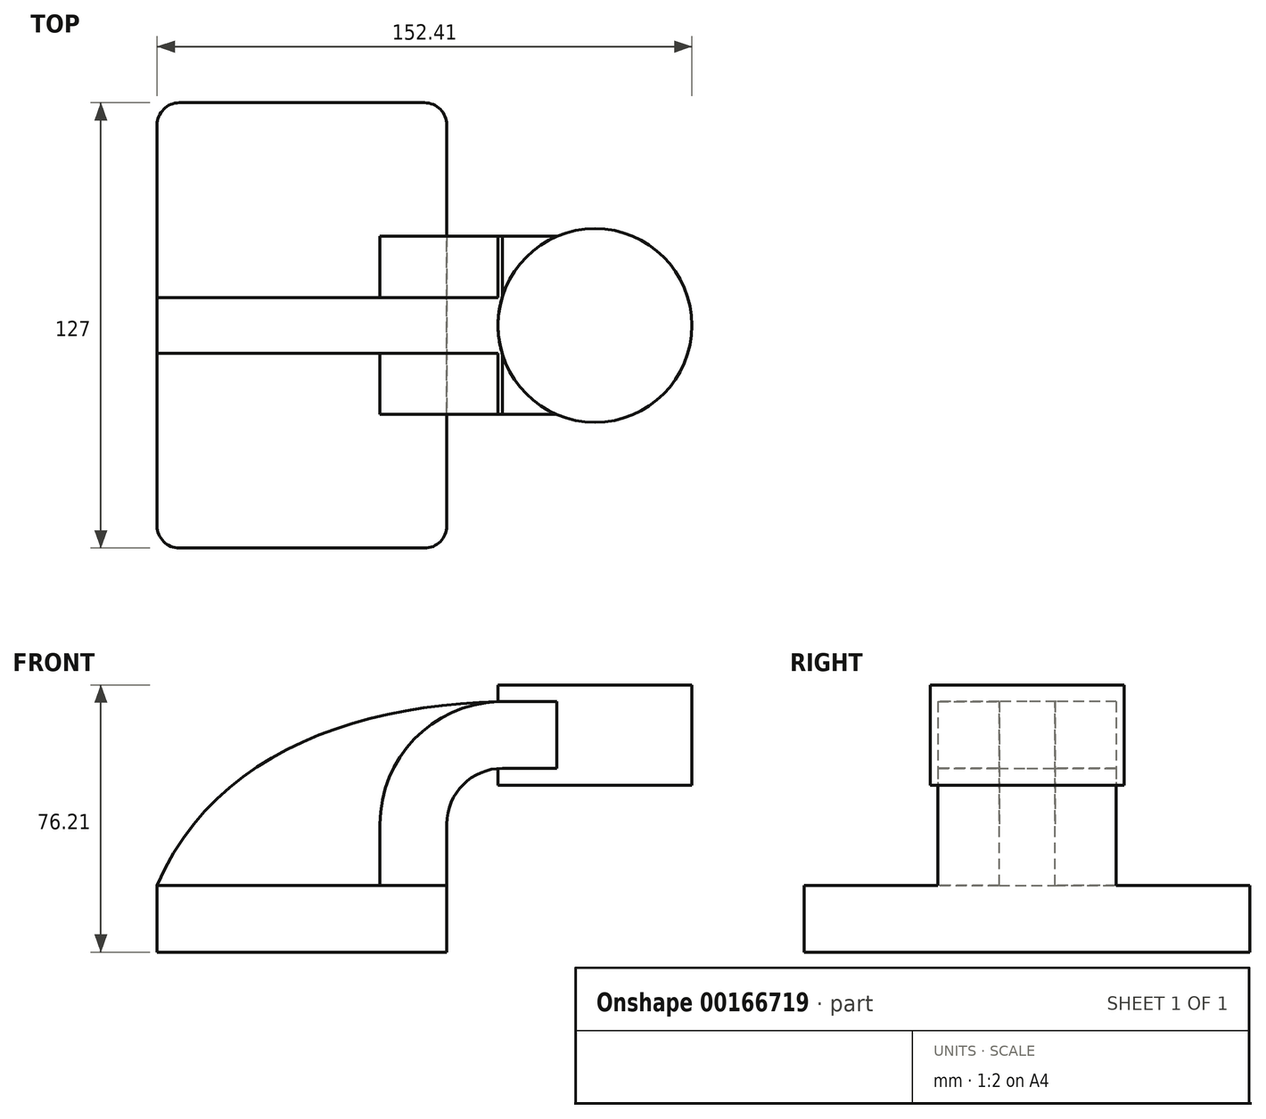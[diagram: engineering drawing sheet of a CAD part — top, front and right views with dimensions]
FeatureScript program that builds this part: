
annotation { "Feature Type Name" : "Feature", "Feature Type Description" : "" }
export const myFeature = defineFeature(function(context is Context, id is Id, definition is map)
    precondition{}
    {
        {
            var Q0;
            Q0=qCreatedBy(makeId("Front.planeOp"),FACE);
            var sketch = newSketch(context, id + "F0", { "sketchPlane" : qUnion([Q0])});
            skLineSegment(sketch, "E0.bottom", {"start": v(-41.28, 9.52) * mm, "end": v(41.27, 9.53) * mm});
            skLineSegment(sketch, "E0.top", {"start": v(-41.28, -9.53) * mm, "end": v(41.28, -9.53) * mm});
            skLineSegment(sketch, "E0.left", {"start": v(-41.28, 9.52) * mm, "end": v(-41.28, -9.53) * mm});
            skLineSegment(sketch, "E0.right", {"start": v(41.28, 9.53) * mm, "end": v(41.28, -9.52) * mm});
            skPoint(sketch, "E0.middle", {"position": v(0, 0) * mm});
            skLineSegment(sketch, "E1.bottom", {"start": v(60.32, 66.68) * mm, "end": v(111.12, 66.68) * mm});
            skLineSegment(sketch, "E1.top", {"start": v(60.32, 38.1) * mm, "end": v(111.12, 38.1) * mm});
            skLineSegment(sketch, "E1.left", {"start": v(60.32, 66.68) * mm, "end": v(60.32, 38.1) * mm});
            skLineSegment(sketch, "E1.right", {"start": v(111.12, 66.68) * mm, "end": v(111.12, 38.1) * mm});
            skPoint(sketch, "E1.middle", {"position": v(85.72, 52.39) * mm});
            skLineSegment(sketch, "E2", {"start": v(41.27, 9.53) * mm, "end": v(41.27, 27) * mm});
            skArc(sketch, "E3", {"start": v(41.27, 27) * mm, "mid": v(45.92, 38.23) * mm, "end": v(57.15, 42.88) * mm});
            skLineSegment(sketch, "E4", {"start": v(57.15, 42.88) * mm, "end": v(83.5, 42.88) * mm});
            skLineSegment(sketch, "E5.0", {"start": v(57.15, 61.93) * mm, "end": v(83.5, 61.93) * mm});
            skArc(sketch, "E5.1", {"start": v(22.22, 27) * mm, "mid": v(32.45, 51.7) * mm, "end": v(57.15, 61.93) * mm});
            skLineSegment(sketch, "E5.2", {"start": v(22.22, 9.53) * mm, "end": v(22.22, 27) * mm});
            skLineSegment(sketch, "E6", {"start": v(83.5, 38.1) * mm, "end": v(83.5, 66.68) * mm});
            skFitSpline(sketch, "E7", {"points": [v(-41.28, 9.52) * mm, v(57.15, 61.93) * mm], "startDerivative": vector(47.97, 112.8) * mm, "endDerivative": vector(123.65, 1.95) * mm});
            skSolve(sketch);
        }
        {
            var Q0;
            Q0=makeQuery(id+"F0.imprint","IMPRINT",FACE,{"disambiguationData":[TD([[makeQuery(id+"F0.imprint","IMPRINT",EDGE,{"derivedFrom":sQuery(id+"F0.wireOp",EDGE,"E0.top")}),1.0]])]});
            extrude(context, id + "F1", {"entities" : qUnion([Q0]), "endBound" : BoundingType.SYMMETRIC, "depth" : 127 * mm});
        }
        {
            var Q0;
            {var subQ0=sQuery(id+"F0.wireOp",EDGE,"E5.0");var subQ1=sQuery(id+"F0.wireOp",EDGE,"E1.left");var subQ2=makeQuery(id+"F0.imprint","INTERSECT",VERTEX,{"derivedFrom":[subQ1,subQ0]});Q0=makeQuery(id+"F0.imprint","IMPRINT",FACE,{"disambiguationData":[TD([[makeQuery(id+"F0.imprint","IMPRINT",EDGE,{"disambiguationData":[TD([[subQ2,-1.0]])],"derivedFrom":subQ1}),1.0]])]});}
            var Q1;
            {var subQ1=sQuery(id+"F0.wireOp",EDGE,"E2");Q1=makeQuery(id+"F0.imprint","IMPRINT",FACE,{"disambiguationData":[TD([[makeQuery(id+"F0.imprint","IMPRINT",EDGE,{"derivedFrom":subQ1}),1.0]])]});}
            extrude(context, id + "F2", {"entities" : qUnion([Q0, Q1]), "operationType" : NewBodyOperationType.ADD, "endBound" : BoundingType.SYMMETRIC, "oppositeDirection" : true, "depth" : 50.8 * mm});
        }
        {
            var Q0;
            {var subQ3=sQuery(id+"F0.wireOp",EDGE,"E5.2");Q0=makeQuery(id+"F0.imprint","IMPRINT",FACE,{"disambiguationData":[TD([[makeQuery(id+"F0.imprint","IMPRINT",EDGE,{"derivedFrom":subQ3}),1.0]])]});}
            extrude(context, id + "F3", {"entities" : qUnion([Q0]), "operationType" : NewBodyOperationType.ADD, "endBound" : BoundingType.SYMMETRIC, "depth" : 15.88 * mm});
        }
        {
            var Q0;
            {var subQ0=sQuery(id+"F0.wireOp",EDGE,"E1.right");Q0=makeQuery(id+"F0.imprint","IMPRINT",FACE,{"disambiguationData":[TD([[makeQuery(id+"F0.imprint","IMPRINT",EDGE,{"derivedFrom":subQ0}),-1.0]])]});}
            var Q1;
            Q1=sQuery(id+"F0.wireOp",EDGE,"E6");
            revolve(context, id + "F4", {"operationType" : NewBodyOperationType.ADD, "entities" : qUnion([Q0]), "axis" : qUnion([Q1]), "revolveType" : RevolveType.FULL});
        }
        {
            var Q0;
            Q0=makeQuery(id+"F1.opExtrude","CAP_EDGE",EDGE,{"disambiguationData":[OSD([sQuery(id+"F0.wireOp",EDGE,"E0.right")])],"isStart":false});
            var Q1;
            Q1=makeQuery(id+"F1.opExtrude","CAP_EDGE",EDGE,{"disambiguationData":[OSD([sQuery(id+"F0.wireOp",EDGE,"E0.left")])],"isStart":false});
            var Q2;
            Q2=makeQuery(id+"F1.opExtrude","CAP_EDGE",EDGE,{"disambiguationData":[OSD([sQuery(id+"F0.wireOp",EDGE,"E0.right")])],"isStart":true});
            var Q3;
            Q3=makeQuery(id+"F1.opExtrude","CAP_EDGE",EDGE,{"disambiguationData":[OSD([sQuery(id+"F0.wireOp",EDGE,"E0.left")])],"isStart":true});
            fillet(context, id + "F5", {"entities" : qUnion([Q0, Q1, Q2, Q3]), "radius" : 6.35 * mm, "tangentPropagation" : true, "allowEdgeOverflow" : false});
        }
    });
